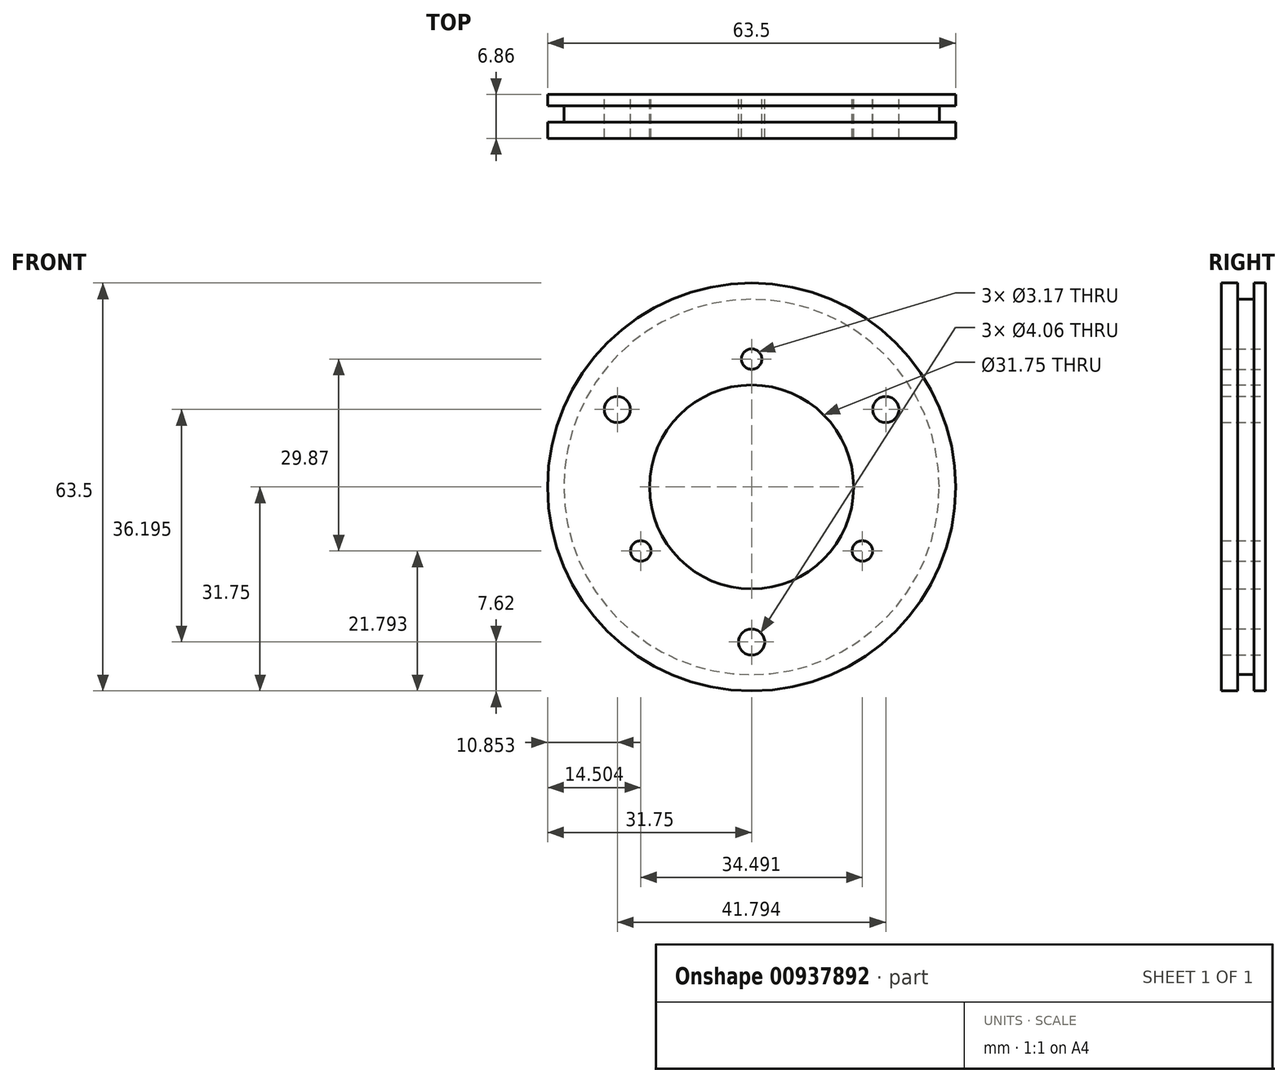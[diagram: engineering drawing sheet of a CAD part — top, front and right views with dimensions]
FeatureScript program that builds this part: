
annotation { "Feature Type Name" : "Feature", "Feature Type Description" : "" }
export const myFeature = defineFeature(function(context is Context, id is Id, definition is map)
    precondition{}
    {
        {
            var Q0;
            Q0=qCreatedBy(makeId("Front.planeOp"),FACE);
            var sketch = newSketch(context, id + "F0", { "sketchPlane" : qUnion([Q0])});
            skCircle(sketch, "E0", {"center": v(0, 0) * mm, "radius": 31.75 * mm});
            skCircle(sketch, "E1", {"center": v(0, 0) * mm, "radius": 15.88 * mm});
            skCircle(sketch, "E2", {"center": v(0, 0) * mm, "radius": 29.21 * mm});
            skPoint(sketch, "E3", {"position": v(0, -24.13) * mm});
            skPoint(sketch, "E4.1.0", {"position": v(20.9, 12.06) * mm});
            skPoint(sketch, "E4.2.0", {"position": v(-20.9, 12.07) * mm});
            skPoint(sketch, "E5", {"position": v(0, 19.91) * mm});
            skPoint(sketch, "E6.1.0", {"position": v(-17.25, -9.96) * mm});
            skPoint(sketch, "E6.2.0", {"position": v(17.25, -9.96) * mm});
            skCircle(sketch, "E7", {"center": v(0, 19.91) * mm, "radius": 1.59 * mm});
            skCircle(sketch, "E8", {"center": v(-17.25, -9.96) * mm, "radius": 1.59 * mm});
            skCircle(sketch, "E9", {"center": v(17.25, -9.96) * mm, "radius": 1.59 * mm});
            skCircle(sketch, "E10", {"center": v(20.9, 12.06) * mm, "radius": 2.03 * mm});
            skCircle(sketch, "E11", {"center": v(-20.9, 12.07) * mm, "radius": 2.03 * mm});
            skCircle(sketch, "E12", {"center": v(0, -24.13) * mm, "radius": 2.03 * mm});
            skSolve(sketch);
        }
        {
            var Q0;
            Q0=makeQuery(id+"F0.imprint","IMPRINT",FACE,{"disambiguationData":[TD([[makeQuery(id+"F0.imprint","IMPRINT",EDGE,{"derivedFrom":sQuery(id+"F0.wireOp",EDGE,"E0")}),1.0]])]});
            var Q1;
            Q1=makeQuery(id+"F0.imprint","IMPRINT",FACE,{"disambiguationData":[TD([[makeQuery(id+"F0.imprint","IMPRINT",EDGE,{"derivedFrom":sQuery(id+"F0.wireOp",EDGE,"E1")}),-1.0]])]});
            extrude(context, id + "F1", {"entities" : qUnion([Q0, Q1]), "depth" : 2.54 * mm, "offsetDistance" : 25.4 * mm});
        }
        {
            var Q0;
            Q0=makeQuery(id+"F1.opExtrude","CAP_FACE",FACE,{"disambiguationData":[OSD([sQuery(id+"F0.wireOp",EDGE,"E0"),sQuery(id+"F0.wireOp",EDGE,"E1"),sQuery(id+"F0.wireOp",EDGE,"E7"),sQuery(id+"F0.wireOp",EDGE,"E8"),sQuery(id+"F0.wireOp",EDGE,"E9"),sQuery(id+"F0.wireOp",EDGE,"E10"),sQuery(id+"F0.wireOp",EDGE,"E11"),sQuery(id+"F0.wireOp",EDGE,"E12")])],"isStart":true});
            var sketch = newSketch(context, id + "F2", { "sketchPlane" : qUnion([Q0])});
            skCircle(sketch, "E13", {"center": v(0, 0) * mm, "radius": 15.88 * mm});
            skCircle(sketch, "E14", {"center": v(0, 0) * mm, "radius": 29.21 * mm});
            skCircle(sketch, "E15", {"center": v(-20.9, 12.06) * mm, "radius": 2.03 * mm});
            skCircle(sketch, "E16", {"center": v(0, 19.91) * mm, "radius": 1.59 * mm});
            skCircle(sketch, "E17", {"center": v(20.9, 12.07) * mm, "radius": 2.03 * mm});
            skCircle(sketch, "E18", {"center": v(17.25, -9.96) * mm, "radius": 1.59 * mm});
            skCircle(sketch, "E19", {"center": v(0, -24.13) * mm, "radius": 2.03 * mm});
            skCircle(sketch, "E20", {"center": v(-17.25, -9.96) * mm, "radius": 1.59 * mm});
            skSolve(sketch);
        }
        {
            var Q0;
            Q0=makeQuery(id+"F2.imprint","IMPRINT",FACE,{"disambiguationData":[TD([[makeQuery(id+"F2.imprint","IMPRINT",EDGE,{"derivedFrom":sQuery(id+"F2.wireOp",EDGE,"E13")}),1.0]])]});
            extrude(context, id + "F3", {"entities" : qUnion([Q0]), "operationType" : NewBodyOperationType.ADD, "depth" : 2.54 * mm, "offsetDistance" : 25.4 * mm});
        }
        {
            var Q0;
            Q0=makeQuery(id+"F3.opExtrude","CAP_FACE",FACE,{"disambiguationData":[OSD([sQuery(id+"F2.wireOp",EDGE,"E13"),sQuery(id+"F2.wireOp",EDGE,"E14"),sQuery(id+"F2.wireOp",EDGE,"E15"),sQuery(id+"F2.wireOp",EDGE,"E16"),sQuery(id+"F2.wireOp",EDGE,"E17"),sQuery(id+"F2.wireOp",EDGE,"E18"),sQuery(id+"F2.wireOp",EDGE,"E19"),sQuery(id+"F2.wireOp",EDGE,"E20")])],"isStart":false});
            var sketch = newSketch(context, id + "F4", { "sketchPlane" : qUnion([Q0])});
            skCircle(sketch, "E21", {"center": v(0, 0) * mm, "radius": 15.88 * mm});
            skCircle(sketch, "E22", {"center": v(0, 0) * mm, "radius": 31.75 * mm});
            skCircle(sketch, "E23", {"center": v(-20.9, 12.06) * mm, "radius": 2.03 * mm});
            skCircle(sketch, "E24", {"center": v(0, 19.91) * mm, "radius": 1.59 * mm});
            skCircle(sketch, "E25", {"center": v(20.9, 12.07) * mm, "radius": 2.03 * mm});
            skCircle(sketch, "E26", {"center": v(17.25, -9.96) * mm, "radius": 1.59 * mm});
            skCircle(sketch, "E27", {"center": v(0, -24.13) * mm, "radius": 2.03 * mm});
            skCircle(sketch, "E28", {"center": v(-17.25, -9.96) * mm, "radius": 1.59 * mm});
            skSolve(sketch);
        }
        {
            var Q0;
            Q0=makeQuery(id+"F4.imprint","IMPRINT",FACE,{"disambiguationData":[TD([[makeQuery(id+"F4.imprint","IMPRINT",EDGE,{"derivedFrom":sQuery(id+"F4.wireOp",EDGE,"E21")}),1.0]])]});
            var Q1;
            Q1=makeQuery(id+"F4.imprint","IMPRINT",FACE,{"disambiguationData":[TD([[makeQuery(id+"F4.imprint","IMPRINT",EDGE,{"derivedFrom":sQuery(id+"F4.wireOp",EDGE,"E22")}),1.0]])]});
            extrude(context, id + "F5", {"entities" : qUnion([Q0, Q1]), "operationType" : NewBodyOperationType.ADD, "depth" : 1.78 * mm, "offsetDistance" : 25.4 * mm});
        }
    });
